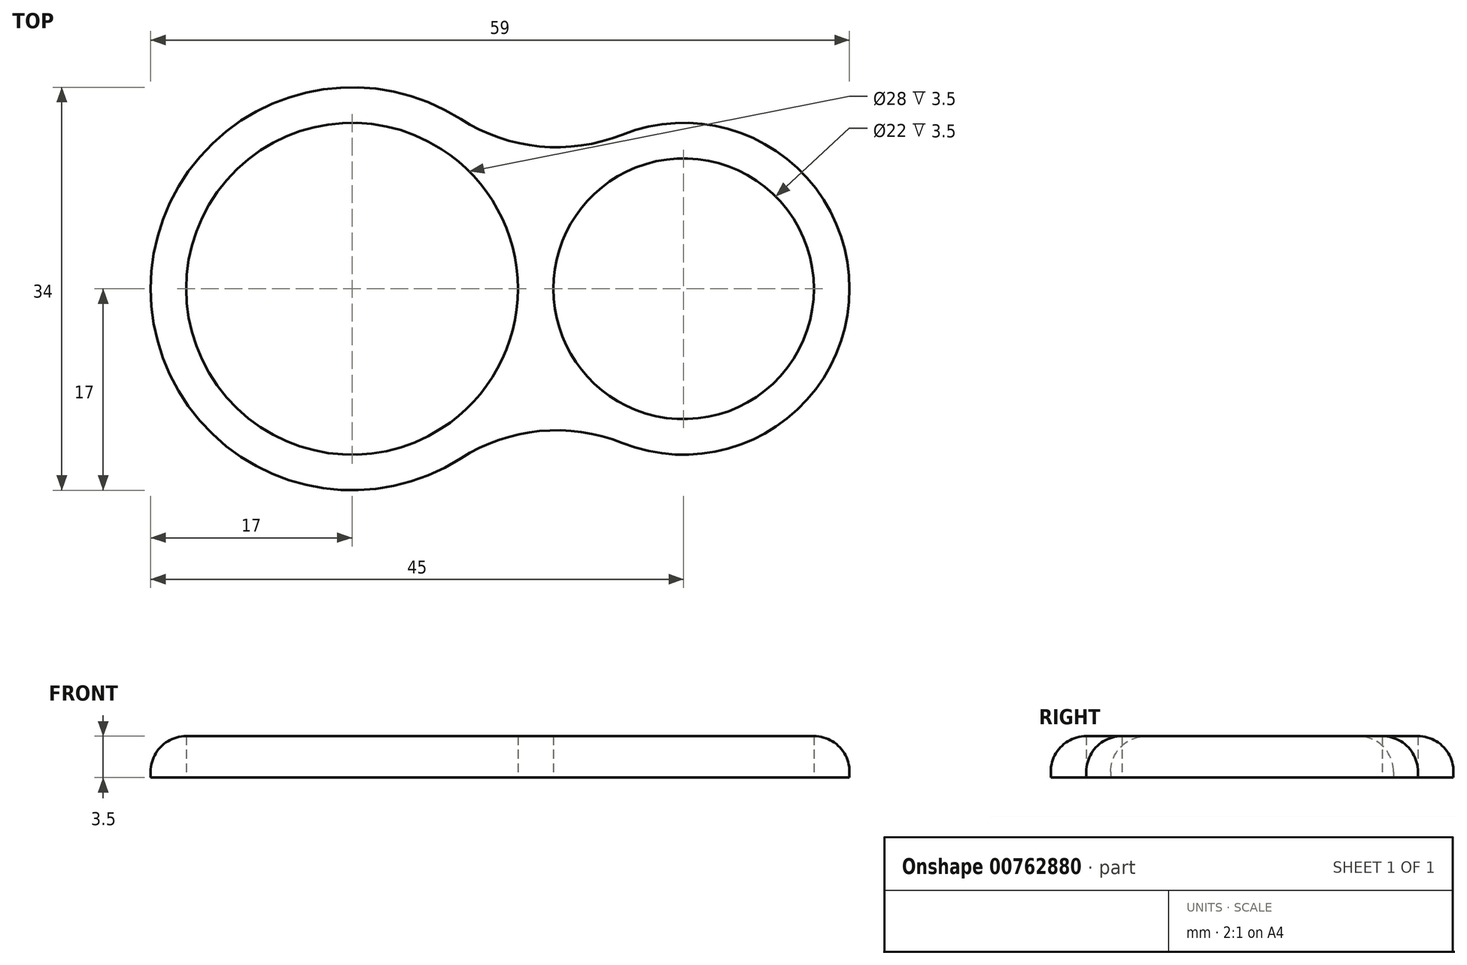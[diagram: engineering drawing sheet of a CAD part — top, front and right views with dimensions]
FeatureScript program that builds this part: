
annotation { "Feature Type Name" : "Feature", "Feature Type Description" : "" }
export const myFeature = defineFeature(function(context is Context, id is Id, definition is map)
    precondition{}
    {
        {
            var Q0;
            Q0=qCreatedBy(makeId("Top.planeOp"),FACE);
            var sketch = newSketch(context, id + "F0", { "sketchPlane" : qUnion([Q0])});
            skCircle(sketch, "E0", {"center": v(0, 0) * mm, "radius": 14 * mm});
            skCircle(sketch, "E1", {"center": v(28, 0) * mm, "radius": 11 * mm});
            skArc(sketch, "E2", {"start": v(9.17, 14.31) * mm, "mid": v(-17, 0) * mm, "end": v(9.17, -14.31) * mm});
            skArc(sketch, "E3", {"start": v(22.82, -13) * mm, "mid": v(42, 0) * mm, "end": v(22.82, 13) * mm});
            skArc(sketch, "E4", {"start": v(9.17, 14.31) * mm, "mid": v(15.84, 12) * mm, "end": v(22.82, 13) * mm});
            skArc(sketch, "E5.MirrorCS", {"start": v(9.17, -14.31) * mm, "mid": v(15.84, -12) * mm, "end": v(22.82, -13) * mm});
            skSolve(sketch);
        }
        {
            var Q0;
            Q0=makeQuery(id+"F0.imprint","IMPRINT",FACE,{"disambiguationData":[TD([[makeQuery(id+"F0.imprint","IMPRINT",EDGE,{"derivedFrom":sQuery(id+"F0.wireOp",EDGE,"E0")}),-1.0]])]});
            extrude(context, id + "F1", {"entities" : qUnion([Q0]), "depth" : 3.5 * mm, "offsetDistance" : 25 * mm});
        }
        {
            var Q0;
            Q0=makeQuery(id+"F1.opExtrude","CAP_EDGE",EDGE,{"disambiguationData":[OSD([sQuery(id+"F0.wireOp",EDGE,"E4")])],"isStart":false});
            fillet(context, id + "F2", {"entities" : qUnion([Q0]), "radius" : 3 * mm, "tangentPropagation" : true, "allowEdgeOverflow" : false});
        }
    });
